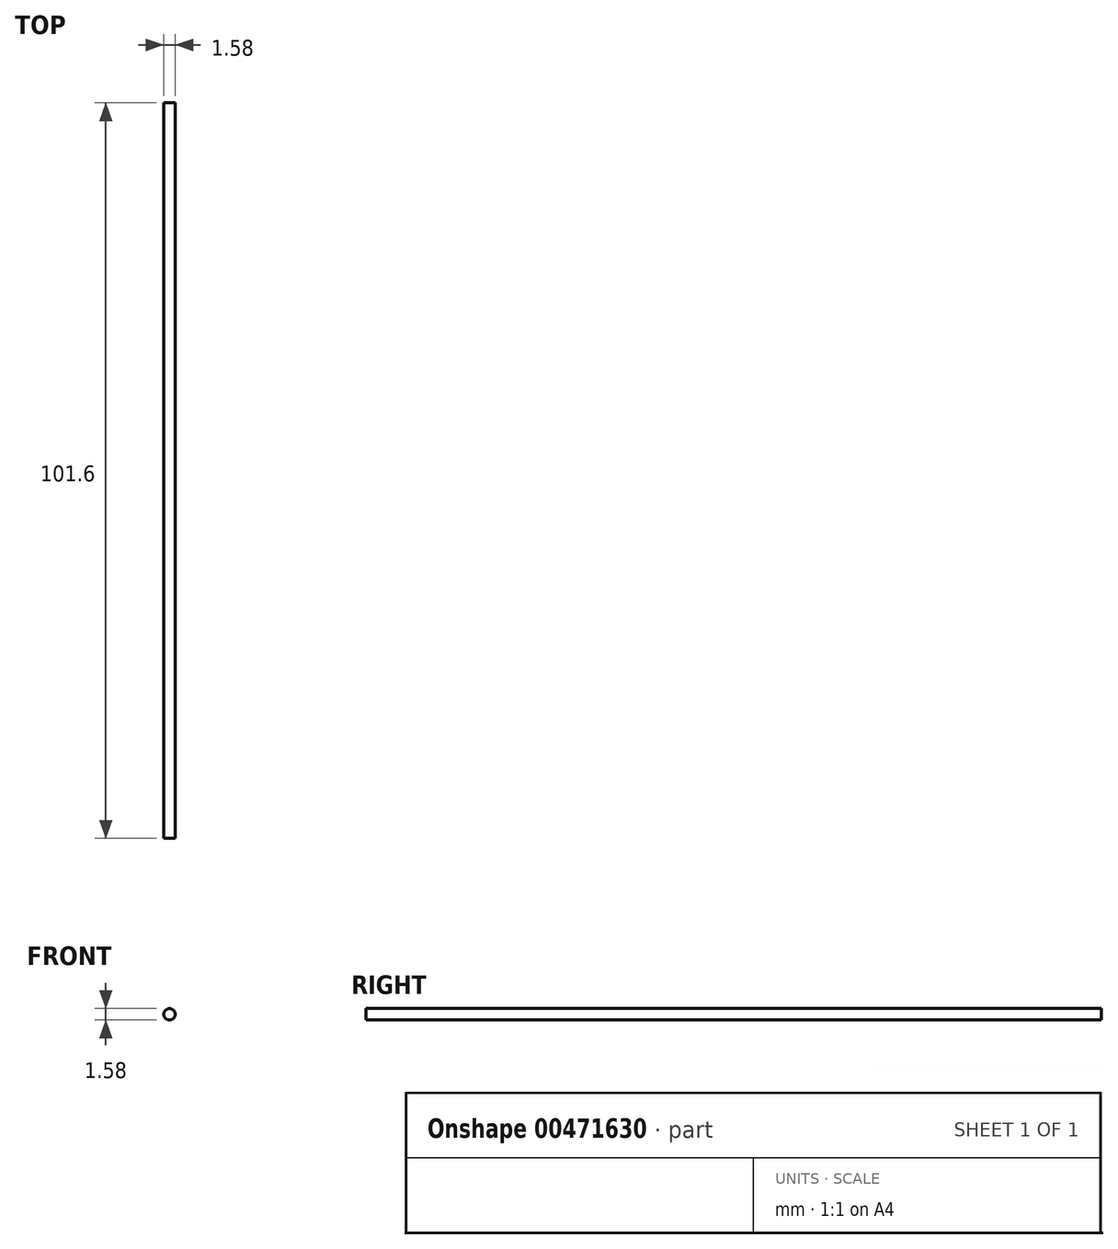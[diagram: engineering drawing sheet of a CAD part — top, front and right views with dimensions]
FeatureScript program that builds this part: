
annotation { "Feature Type Name" : "Feature", "Feature Type Description" : "" }
export const myFeature = defineFeature(function(context is Context, id is Id, definition is map)
    precondition{}
    {
        {
            var Q0;
            Q0=qCreatedBy(makeId("Front.planeOp"),FACE);
            var sketch = newSketch(context, id + "F0", { "sketchPlane" : qUnion([Q0])});
            skCircle(sketch, "E0", {"center": v(0, 0) * mm, "radius": 0.8 * mm});
            skSolve(sketch);
        }
        {
            var Q0;
            Q0 = qSketchRegion(id + "F0", true);
            extrude(context, id + "F1", {"entities" : qUnion([Q0]), "depth" : 101.6 * mm});
        }
    });
